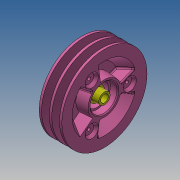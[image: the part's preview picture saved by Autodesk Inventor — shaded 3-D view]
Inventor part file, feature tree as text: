
AUTODESK INVENTOR PART (.ipt)
format: ipt  version: 2017 (Build 210142000, 142)  size: 558,592 bytes
history: native  units: mm
features: revolve x5, other x4, chamfer x4, extrude x3, sketch x2, plane x2, fillet x1, pattern_circular x1, split x1
ambient origin geometry x8: Origin, YZ Plane, XZ Plane, XY Plane, X Axis, Y Axis, Z Axis, Center Point
bodies: Body1 (feature_tree), Body2 (feature_tree), Body3 (feature_tree)
feature tree (23):
  other  "Sólido1"
  sketch  "Boceto1"  dims[d0=8.0mm d1=28.5mm]
  revolve  "Revolución1"  [1 undecoded]
  sketch  "Boceto2"  dims[d2=24.5mm d3=8.0mm d4=4.0mm d5=90.0mm d6=20.0mm d7=2.5mm d8=90.0deg d10=9.0mm d11=3.0mm d13=52.5mm d14=10.0mm d15=0.0mm d16=10.0mm d17=0.0mm d18=8.0mm d24=44.5mm d25=49.5mm d26=8.0mm d27=12.0mm d28=16.0mm d29=8.0mm d30=90.0deg d31=24.0mm d32=32.0mm d33=20.0mm d34=8.281806mm d35=3.0mm d36=0.0mm d37=60.0deg d39=1.5mm d40=30.0mm d41=360.0deg d43=60.0deg d44=1.5mm d45=90.0deg d46=1.0mm d47=2.0mm d48=45.0deg d49=2.0mm d50=3.0mm d51=45.0deg d52=4.0mm d53=70.0mm d54=3.0mm d55=90.0deg d56=120.0deg d59=12.0mm d60=2.0mm d61=17.453293mm d65=7.0mm d66=3.0mm d67=7.0mm d68=7.0mm d69=10.0mm d70=45.0deg d71=12.0mm d72=12.0mm d73=2.0mm d74=17.453293mm d75=30.0deg d76=30.0deg]
  extrude  "Extrusión1"  Depth=8.0mm
  chamfer  "Chaflán1"  Distance=4.0mm
  revolve  "Revolución6"  [1 undecoded]
  plane  "Plano de trabajo1"
  extrude  "Extrusión2"  Depth=10.0mm
  extrude  "Extrusión3"  TaperAngle=90.0deg  [1 undecoded]
  chamfer  "Chaflán2"  Distance=9.0mm
  chamfer  "Chaflán3"  Distance=3.0mm
  chamfer  "Chaflán5"  Distance=52.5mm
  fillet  "Empalme1"  Radius=10.0mm
  pattern_circular  "Patrón circular1"  [2 undecoded]
  plane  "Plano de trabajo2"
  revolve  "Revolución4"  [1 undecoded]
  revolve  "Revolución5"  [1 undecoded]
  revolve  "Revolución2"  [1 undecoded]
  split  "Dividir1"
  other  "espaciador"
  other  "Sólido3"
  other  "Sólido4"
note: 8 required parameter values undecoded (feature->parameter linkage not recoverable at this tier; creation-order binding heuristic only, values carry confidence <= 0.55)